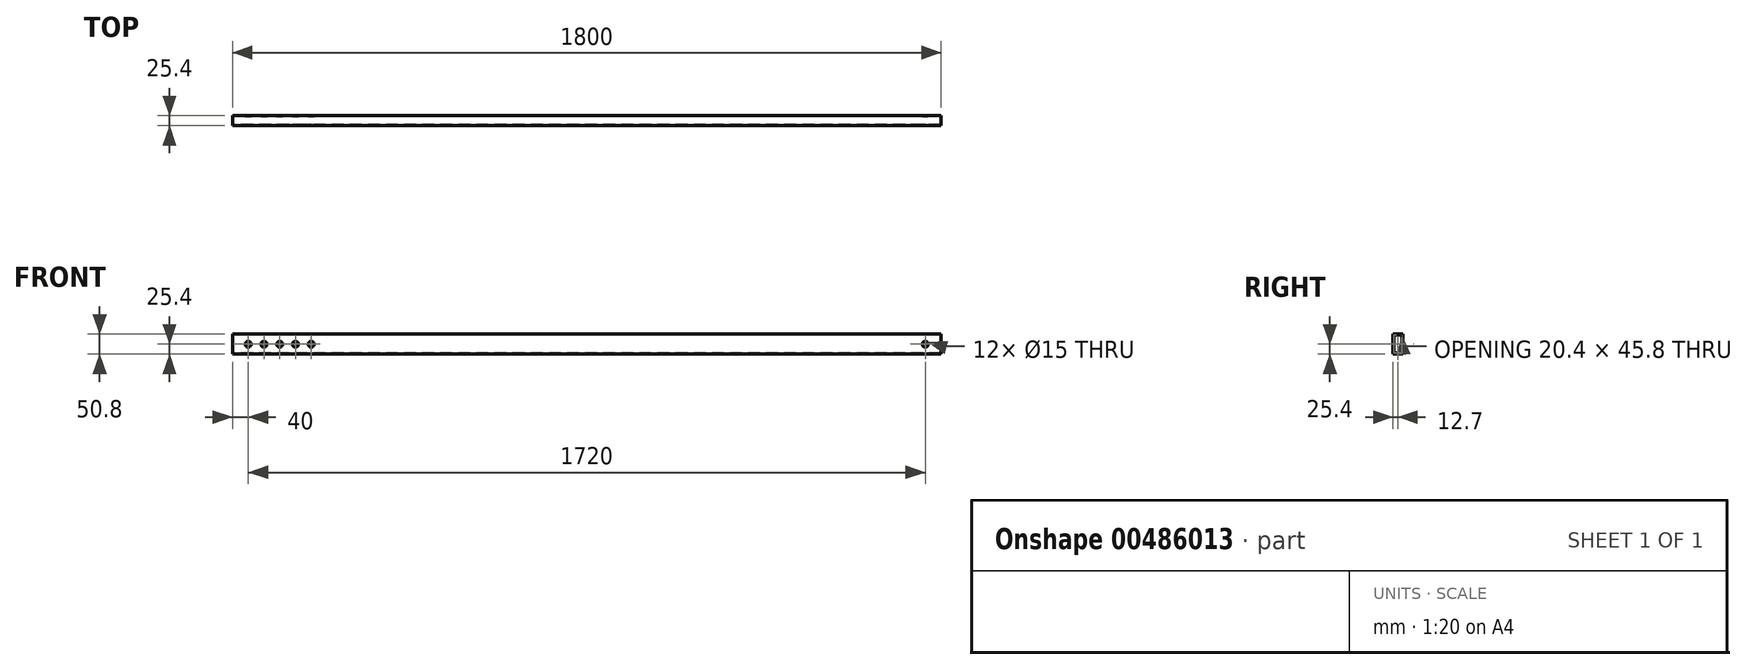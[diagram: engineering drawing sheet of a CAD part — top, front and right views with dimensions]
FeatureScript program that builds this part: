
annotation { "Feature Type Name" : "Feature", "Feature Type Description" : "" }
export const myFeature = defineFeature(function(context is Context, id is Id, definition is map)
    precondition{}
    {
        {
            var Q0;
            Q0=qCreatedBy(makeId("Right.planeOp"),FACE);
            var sketch = newSketch(context, id + "F0", { "sketchPlane" : qUnion([Q0])});
            skLineSegment(sketch, "E0.bottom", {"start": v(12.7, 25.4) * mm, "end": v(-12.7, 25.4) * mm});
            skLineSegment(sketch, "E0.top", {"start": v(12.7, -25.4) * mm, "end": v(-12.7, -25.4) * mm});
            skLineSegment(sketch, "E0.left", {"start": v(12.7, 25.4) * mm, "end": v(12.7, -25.4) * mm});
            skLineSegment(sketch, "E0.right", {"start": v(-12.7, 25.4) * mm, "end": v(-12.7, -25.4) * mm});
            skPoint(sketch, "E0.middle", {"position": v(0, 0) * mm});
            skLineSegment(sketch, "E1.bottom", {"start": v(8.2, 22.9) * mm, "end": v(-8.2, 22.9) * mm});
            skLineSegment(sketch, "E1.top", {"start": v(8.2, -22.9) * mm, "end": v(-8.2, -22.9) * mm});
            skLineSegment(sketch, "E1.left", {"start": v(10.2, 20.9) * mm, "end": v(10.2, -20.9) * mm});
            skLineSegment(sketch, "E1.right", {"start": v(-10.2, 20.9) * mm, "end": v(-10.2, -20.9) * mm});
            skPoint(sketch, "E2.visualSharp", {"position": v(-10.2, 22.9) * mm});
            skArc(sketch, "E2.filletArc", {"start": v(-8.2, 22.9) * mm, "mid": v(-9.61, 22.31) * mm, "end": v(-10.2, 20.9) * mm});
            skPoint(sketch, "E3.visualSharp", {"position": v(10.2, 22.9) * mm});
            skArc(sketch, "E3.filletArc", {"start": v(10.2, 20.9) * mm, "mid": v(9.61, 22.31) * mm, "end": v(8.2, 22.9) * mm});
            skPoint(sketch, "E4.visualSharp", {"position": v(-10.2, -22.9) * mm});
            skArc(sketch, "E4.filletArc", {"start": v(-10.2, -20.9) * mm, "mid": v(-9.61, -22.31) * mm, "end": v(-8.2, -22.9) * mm});
            skPoint(sketch, "E5.visualSharp", {"position": v(10.2, -22.9) * mm});
            skArc(sketch, "E5.filletArc", {"start": v(8.2, -22.9) * mm, "mid": v(9.61, -22.31) * mm, "end": v(10.2, -20.9) * mm});
            skPoint(sketch, "E6.visualSharp", {"position": v(-12.7, -25.4) * mm});
            skSolve(sketch);
        }
        {
            var Q0;
            Q0 = qSketchRegion(id + "F0", true);
            extrude(context, id + "F1", {"entities" : qUnion([Q0]), "depth" : 1800 * mm});
        }
        {
            var Q0;
            Q0=makeQuery(id+"F1.opExtrude","SWEPT_FACE",FACE,{"disambiguationData":[OSD([sQuery(id+"F0.wireOp",EDGE,"E0.right")])]});
            var sketch = newSketch(context, id + "F2", { "sketchPlane" : qUnion([Q0])});
            skCircle(sketch, "E7", {"center": v(1760, 0) * mm, "radius": 7.5 * mm});
            skSolve(sketch);
        }
        {
            var Q0;
            Q0 = qSketchRegion(id + "F2", true);
            var Q1;
            Q1=makeQuery(id+"F1.opExtrude","SWEPT_FACE",FACE,{"disambiguationData":[OSD([sQuery(id+"F0.wireOp",EDGE,"E0.left")])]});
            extrude(context, id + "F3", {"entities" : qUnion([Q0]), "operationType" : NewBodyOperationType.REMOVE, "endBound" : BoundingType.UP_TO_SURFACE, "oppositeDirection" : true, "endBoundEntityFace" : qUnion([Q1]), "depth" : 25 * mm});
        }
        {
            var Q0;
            Q0=makeQuery(id+"F1.opExtrude","SWEPT_FACE",FACE,{"disambiguationData":[OSD([sQuery(id+"F0.wireOp",EDGE,"E0.right")])]});
            var sketch = newSketch(context, id + "F4", { "sketchPlane" : qUnion([Q0])});
            skCircle(sketch, "E8", {"center": v(40, 0) * mm, "radius": 7.5 * mm});
            skCircle(sketch, "E9", {"center": v(80, 0) * mm, "radius": 7.5 * mm});
            skCircle(sketch, "E10", {"center": v(120, 0) * mm, "radius": 7.5 * mm});
            skCircle(sketch, "E11", {"center": v(160, 0) * mm, "radius": 7.5 * mm});
            skCircle(sketch, "E12", {"center": v(200, 0) * mm, "radius": 7.5 * mm});
            skCircle(sketch, "E13", {"center": v(240, 0) * mm, "radius": 7.5 * mm});
            skCircle(sketch, "E14", {"center": v(280, 0) * mm, "radius": 7.5 * mm});
            skCircle(sketch, "E15", {"center": v(320, 0) * mm, "radius": 7.5 * mm});
            skCircle(sketch, "E16", {"center": v(360, 0) * mm, "radius": 7.5 * mm});
            skCircle(sketch, "E17", {"center": v(400, 0) * mm, "radius": 7.5 * mm});
            skSolve(sketch);
        }
        {
            var Q0;
            Q0=makeQuery(id+"F4.imprint","IMPRINT",FACE,{"disambiguationData":[TD([[makeQuery(id+"F4.imprint","IMPRINT",EDGE,{"derivedFrom":sQuery(id+"F4.wireOp",EDGE,"E8")}),1.0]])]});
            var Q1;
            Q1=makeQuery(id+"F4.imprint","IMPRINT",FACE,{"disambiguationData":[TD([[makeQuery(id+"F4.imprint","IMPRINT",EDGE,{"derivedFrom":sQuery(id+"F4.wireOp",EDGE,"E9")}),1.0]])]});
            var Q2;
            Q2=makeQuery(id+"F4.imprint","IMPRINT",FACE,{"disambiguationData":[TD([[makeQuery(id+"F4.imprint","IMPRINT",EDGE,{"derivedFrom":sQuery(id+"F4.wireOp",EDGE,"E10")}),1.0]])]});
            var Q3;
            Q3=makeQuery(id+"F4.imprint","IMPRINT",FACE,{"disambiguationData":[TD([[makeQuery(id+"F4.imprint","IMPRINT",EDGE,{"derivedFrom":sQuery(id+"F4.wireOp",EDGE,"E11")}),1.0]])]});
            var Q4;
            Q4=makeQuery(id+"F4.imprint","IMPRINT",FACE,{"disambiguationData":[TD([[makeQuery(id+"F4.imprint","IMPRINT",EDGE,{"derivedFrom":sQuery(id+"F4.wireOp",EDGE,"E12")}),1.0]])]});
            var Q5;
            Q5=makeQuery(id+"F1.opExtrude","SWEPT_FACE",FACE,{"disambiguationData":[OSD([sQuery(id+"F0.wireOp",EDGE,"E0.left")])]});
            extrude(context, id + "F5", {"entities" : qUnion([Q0, Q1, Q2, Q3, Q4]), "operationType" : NewBodyOperationType.REMOVE, "endBound" : BoundingType.UP_TO_SURFACE, "oppositeDirection" : true, "endBoundEntityFace" : qUnion([Q5]), "depth" : 25 * mm});
        }
    });
